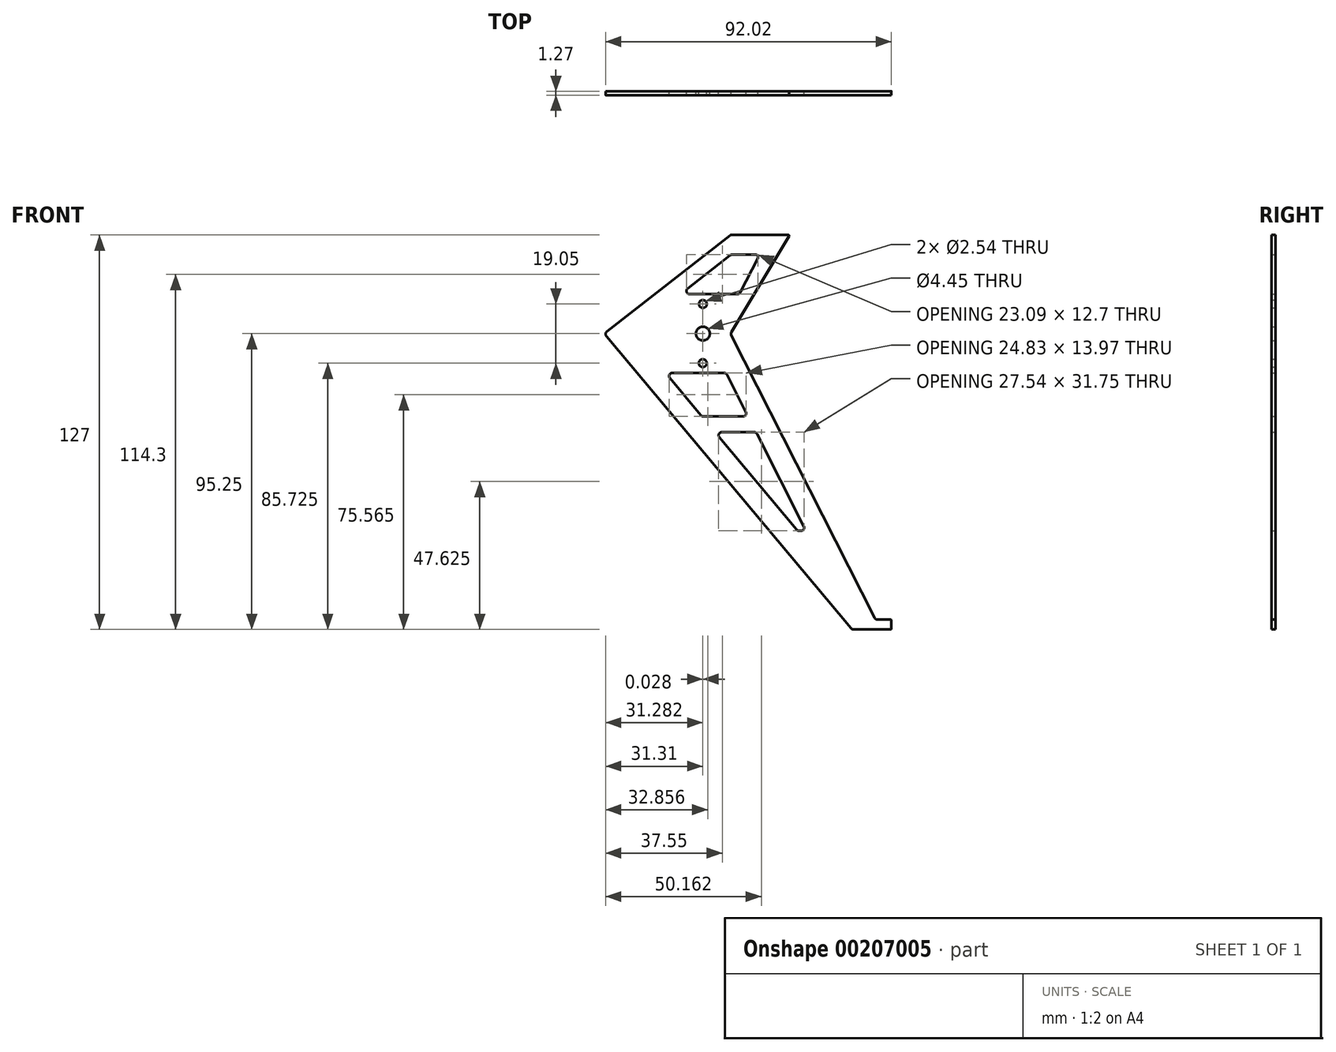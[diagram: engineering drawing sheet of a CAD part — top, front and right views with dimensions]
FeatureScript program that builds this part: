
annotation { "Feature Type Name" : "Feature", "Feature Type Description" : "" }
export const myFeature = defineFeature(function(context is Context, id is Id, definition is map)
    precondition{}
    {
        {
            var Q0;
            Q0=qCreatedBy(makeId("Front.planeOp"),FACE);
            var sketch = newSketch(context, id + "F0", { "sketchPlane" : qUnion([Q0])});
            skLineSegment(sketch, "E0", {"start": v(-3.72, 63.5) * mm, "end": v(14.8, 63.5) * mm});
            skLineSegment(sketch, "E1", {"start": v(35.78, -63.5) * mm, "end": v(44.45, -63.5) * mm});
            skLineSegment(sketch, "E2", {"start": v(-43.62, 32.4) * mm, "end": v(-3.88, 63.45) * mm});
            skPoint(sketch, "E3", {"position": v(15.24, 63.5) * mm});
            skPoint(sketch, "E4", {"position": v(-3.8, 31.75) * mm});
            skLineSegment(sketch, "E5", {"start": v(15, 63.12) * mm, "end": v(-3.52, 32.23) * mm});
            skLineSegment(sketch, "E6", {"start": v(-3.56, 31.25) * mm, "end": v(42.56, -59.77) * mm});
            skLineSegment(sketch, "E7", {"start": v(43.47, -60.33) * mm, "end": v(47.75, -60.33) * mm});
            skLineSegment(sketch, "E8", {"start": v(48, -60.58) * mm, "end": v(48, -63.25) * mm});
            skLineSegment(sketch, "E9", {"start": v(47.75, -63.5) * mm, "end": v(44.45, -63.5) * mm});
            skPoint(sketch, "E10", {"position": v(35.3, -63.5) * mm});
            skLineSegment(sketch, "E11", {"start": v(-43.78, 30.94) * mm, "end": v(35, -63.14) * mm});
            skLineSegment(sketch, "E12.0", {"start": v(-4.9, 18.5) * mm, "end": v(1.15, 6.56) * mm});
            skLineSegment(sketch, "E13.0", {"start": v(-39.11, 36.22) * mm, "end": v(-38.96, 36.04) * mm});
            skLineSegment(sketch, "E14.0", {"start": v(-41.32, 27.75) * mm, "end": v(-41.19, 27.85) * mm});
            skLineSegment(sketch, "E15.0", {"start": v(-3.34, 57.15) * mm, "end": v(4.33, 57.15) * mm});
            skLineSegment(sketch, "E16.trimOffspring", {"start": v(5, 56.04) * mm, "end": v(-0.65, 45) * mm});
            skLineSegment(sketch, "E17.trimOffspring", {"start": v(-17.62, 46.27) * mm, "end": v(-3.96, 56.93) * mm});
            skLineSegment(sketch, "E18.trimOffspring", {"start": v(-23.34, 17.38) * mm, "end": v(-13.35, 5.44) * mm});
            skLineSegment(sketch, "E19.trimOffspring", {"start": v(18.27, -31.75) * mm, "end": v(18.9, -31.75) * mm});
            skLineSegment(sketch, "E20", {"start": v(-6.61, 0) * mm, "end": v(3.85, 0) * mm});
            skLineSegment(sketch, "E21", {"start": v(-12.57, 5.08) * mm, "end": v(0.25, 5.08) * mm});
            skLineSegment(sketch, "E22.trimOffspring", {"start": v(4.76, -0.56) * mm, "end": v(19.81, -30.27) * mm});
            skLineSegment(sketch, "E23.trimOffspring", {"start": v(-7.4, -1.67) * mm, "end": v(17.5, -31.39) * mm});
            skCircle(sketch, "E24", {"center": v(-12.7, 31.75) * mm, "radius": 2.22 * mm});
            skCircle(sketch, "E25", {"center": v(-12.7, 41.27) * mm, "radius": 1.27 * mm});
            skCircle(sketch, "E26", {"center": v(-12.73, 22.23) * mm, "radius": 1.27 * mm});
            skLineSegment(sketch, "E27", {"start": v(-22.56, 19.05) * mm, "end": v(-5.8, 19.05) * mm});
            skLineSegment(sketch, "E28", {"start": v(-17, 44.45) * mm, "end": v(-1.55, 44.45) * mm});
            skPoint(sketch, "E29.visualSharp", {"position": v(5.57, 57.15) * mm});
            skArc(sketch, "E29.filletArc", {"start": v(5, 56.04) * mm, "mid": v(4.98, 56.79) * mm, "end": v(4.33, 57.15) * mm});
            skArc(sketch, "E30.filletArc", {"start": v(-3.34, 57.15) * mm, "mid": v(-3.67, 57.1) * mm, "end": v(-3.96, 56.93) * mm});
            skPoint(sketch, "E31.visualSharp", {"position": v(-19.94, 44.45) * mm});
            skArc(sketch, "E31.filletArc", {"start": v(-17.62, 46.27) * mm, "mid": v(-17.95, 45.14) * mm, "end": v(-17, 44.45) * mm});
            skPoint(sketch, "E32.visualSharp", {"position": v(-0.93, 44.45) * mm});
            skArc(sketch, "E32.filletArc", {"start": v(-1.55, 44.45) * mm, "mid": v(-1.02, 44.6) * mm, "end": v(-0.65, 45) * mm});
            skArc(sketch, "E33.filletArc", {"start": v(-3.52, 32.23) * mm, "mid": v(-3.67, 31.74) * mm, "end": v(-3.56, 31.25) * mm});
            skPoint(sketch, "E34.visualSharp", {"position": v(-44.45, 31.75) * mm});
            skArc(sketch, "E34.filletArc", {"start": v(-43.62, 32.4) * mm, "mid": v(-44, 31.7) * mm, "end": v(-43.78, 30.94) * mm});
            skPoint(sketch, "E35.visualSharp", {"position": v(-24.74, 19.05) * mm});
            skArc(sketch, "E35.filletArc", {"start": v(-22.56, 19.05) * mm, "mid": v(-23.48, 18.46) * mm, "end": v(-23.34, 17.38) * mm});
            skPoint(sketch, "E36.visualSharp", {"position": v(-5.18, 19.05) * mm});
            skArc(sketch, "E36.filletArc", {"start": v(-4.9, 18.5) * mm, "mid": v(-5.27, 18.9) * mm, "end": v(-5.8, 19.05) * mm});
            skPoint(sketch, "E37.visualSharp", {"position": v(1.9, 5.08) * mm});
            skArc(sketch, "E37.filletArc", {"start": v(0.25, 5.08) * mm, "mid": v(1.11, 5.56) * mm, "end": v(1.15, 6.56) * mm});
            skPoint(sketch, "E38.visualSharp", {"position": v(-13.04, 5.08) * mm});
            skArc(sketch, "E38.filletArc", {"start": v(-13.35, 5.44) * mm, "mid": v(-13, 5.18) * mm, "end": v(-12.57, 5.08) * mm});
            skPoint(sketch, "E39.visualSharp", {"position": v(-8.79, 0) * mm});
            skArc(sketch, "E39.filletArc", {"start": v(-6.61, 0) * mm, "mid": v(-7.53, -0.59) * mm, "end": v(-7.4, -1.67) * mm});
            skPoint(sketch, "E40.visualSharp", {"position": v(4.47, 0) * mm});
            skArc(sketch, "E40.filletArc", {"start": v(4.76, -0.56) * mm, "mid": v(4.38, -0.15) * mm, "end": v(3.85, 0) * mm});
            skPoint(sketch, "E41.visualSharp", {"position": v(17.8, -31.75) * mm});
            skArc(sketch, "E41.filletArc", {"start": v(17.5, -31.39) * mm, "mid": v(17.84, -31.65) * mm, "end": v(18.27, -31.75) * mm});
            skPoint(sketch, "E42.visualSharp", {"position": v(20.56, -31.75) * mm});
            skArc(sketch, "E42.filletArc", {"start": v(18.9, -31.75) * mm, "mid": v(19.77, -31.27) * mm, "end": v(19.81, -30.27) * mm});
            skPoint(sketch, "E43.visualSharp", {"position": v(42.84, -60.33) * mm});
            skArc(sketch, "E43.filletArc", {"start": v(42.56, -59.77) * mm, "mid": v(42.93, -60.17) * mm, "end": v(43.47, -60.33) * mm});
            skArc(sketch, "E44.filletArc", {"start": v(35, -63.14) * mm, "mid": v(35.35, -63.4) * mm, "end": v(35.78, -63.5) * mm});
            skPoint(sketch, "E45.visualSharp", {"position": v(48, -60.33) * mm});
            skArc(sketch, "E45.filletArc", {"start": v(48, -60.58) * mm, "mid": v(47.93, -60.4) * mm, "end": v(47.75, -60.33) * mm});
            skPoint(sketch, "E46.visualSharp", {"position": v(48, -63.5) * mm});
            skArc(sketch, "E46.filletArc", {"start": v(47.75, -63.5) * mm, "mid": v(47.93, -63.43) * mm, "end": v(48, -63.25) * mm});
            skArc(sketch, "E47.filletArc", {"start": v(15, 63.12) * mm, "mid": v(15.01, 63.37) * mm, "end": v(14.8, 63.5) * mm});
            skPoint(sketch, "E48.visualSharp", {"position": v(-3.8, 63.5) * mm});
            skArc(sketch, "E48.filletArc", {"start": v(-3.72, 63.5) * mm, "mid": v(-3.8, 63.49) * mm, "end": v(-3.88, 63.45) * mm});
            skSolve(sketch);
        }
        {
            var Q0;
            Q0 = qSketchRegion(id + "F0", true);
            extrude(context, id + "F1", {"entities" : qUnion([Q0]), "depth" : 1.27 * mm});
        }
    });
